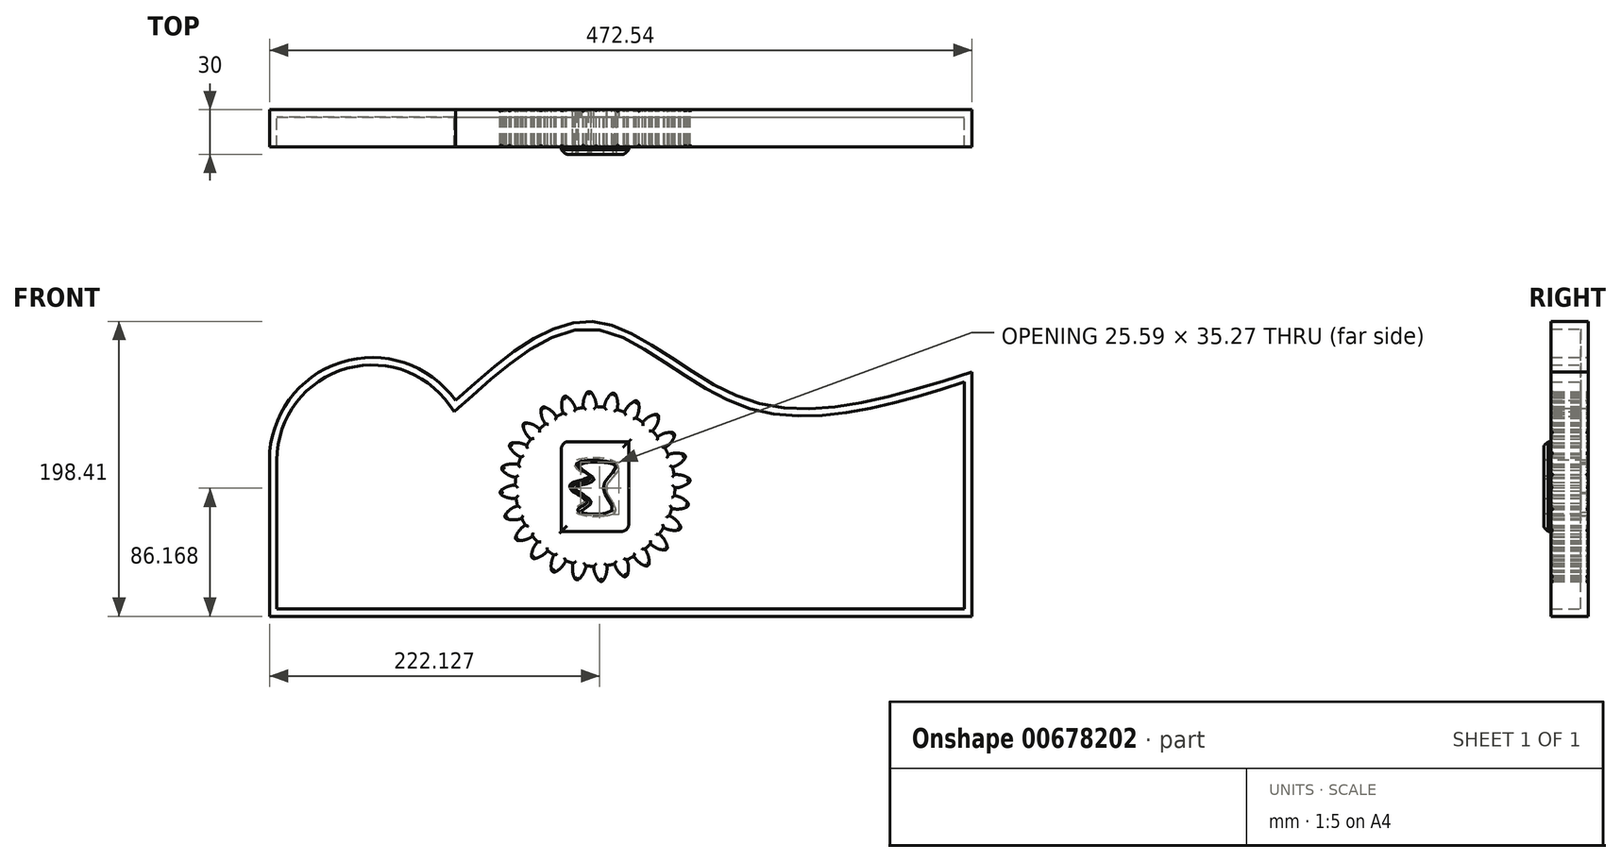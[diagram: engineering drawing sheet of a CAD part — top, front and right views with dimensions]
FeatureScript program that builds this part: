
annotation { "Feature Type Name" : "Feature", "Feature Type Description" : "" }
export const myFeature = defineFeature(function(context is Context, id is Id, definition is map)
    precondition{}
    {
        {
            var Q0;
            Q0=qCreatedBy(makeId("Front.planeOp"),FACE);
            var sketch = newSketch(context, id + "F0", { "sketchPlane" : qUnion([Q0])});
            skCircle(sketch, "E0", {"center": v(0, 0) * mm, "radius": 53.72 * mm});
            skCircle(sketch, "E1", {"center": v(0, 0) * mm, "radius": 58.67 * mm, "construction": true});
            skCircle(sketch, "E2", {"center": v(0, 0) * mm, "radius": 63.5 * mm, "construction": true});
            skLineSegment(sketch, "E3", {"start": v(0, 0) * mm, "end": v(0, 95.08) * mm, "construction": true});
            skLineSegment(sketch, "E4", {"start": v(0, 0) * mm, "end": v(-6.3, 96.03) * mm, "construction": true});
            skLineSegment(sketch, "E5", {"start": v(0, 63.95) * mm, "end": v(0, 63.5) * mm, "construction": true});
            skLineSegment(sketch, "E6", {"start": v(0, 58.67) * mm, "end": v(-63.97, 58.67) * mm, "construction": true});
            skLineSegment(sketch, "E7", {"start": v(0, 58.67) * mm, "end": v(-64.16, 35.32) * mm, "construction": true});
            skCircle(sketch, "E8", {"center": v(0, 0) * mm, "radius": 55.14 * mm, "construction": true});
            skCircle(sketch, "E9", {"center": v(0, 58.67) * mm, "radius": 14.6 * mm, "construction": true});
            skCircle(sketch, "E10", {"center": v(-13.72, 53.68) * mm, "radius": 14.6 * mm, "construction": true});
            skArc(sketch, "E11", {"start": v(0, 58.67) * mm, "mid": v(-1.2, 61.2) * mm, "end": v(-2.86, 63.44) * mm});
            skArc(sketch, "E12", {"start": v(0.88, 53.71) * mm, "mid": v(0.66, 56.23) * mm, "end": v(0, 58.67) * mm});
            skArc(sketch, "E13.MirrorCS", {"start": v(-7.66, 58.17) * mm, "mid": v(-6.8, 60.83) * mm, "end": v(-5.45, 63.27) * mm});
            skArc(sketch, "E14.MirrorCS", {"start": v(-7.88, 53.14) * mm, "mid": v(-7.99, 55.67) * mm, "end": v(-7.66, 58.17) * mm});
            skArc(sketch, "E15", {"start": v(-2.86, 63.44) * mm, "mid": v(-4.18, 63.85) * mm, "end": v(-5.45, 63.27) * mm});
            skLineSegment(sketch, "E16.bottom", {"start": v(22.6, 30.17) * mm, "end": v(-18.1, 30.17) * mm});
            skLineSegment(sketch, "E16.top", {"start": v(18.1, -30.17) * mm, "end": v(-22.6, -30.17) * mm});
            skLineSegment(sketch, "E16.left", {"start": v(22.6, 30.17) * mm, "end": v(22.6, -25.67) * mm});
            skLineSegment(sketch, "E16.right", {"start": v(-22.6, 25.67) * mm, "end": v(-22.6, -30.17) * mm});
            skFitSpline(sketch, "E17", {"points": [v(-11.69, -16.1) * mm, v(11.42, -16.15) * mm, v(5.58, 0) * mm, v(13.67, 14.65) * mm, v(-12.75, 15.4) * mm, v(-2.8, 5.83) * mm, v(-15.25, 0) * mm, v(-4.75, -9.12) * mm, v(-11.69, -16.1) * mm]});
            skPoint(sketch, "E18.visualSharp", {"position": v(-22.6, 30.17) * mm});
            skArc(sketch, "E18.filletArc", {"start": v(-18.1, 30.17) * mm, "mid": v(-21.28, 28.85) * mm, "end": v(-22.6, 25.67) * mm});
            skPoint(sketch, "E19.visualSharp", {"position": v(22.6, -30.17) * mm});
            skArc(sketch, "E19.filletArc", {"start": v(18.1, -30.17) * mm, "mid": v(21.28, -28.85) * mm, "end": v(22.6, -25.67) * mm});
            skSolve(sketch);
        }
        {
            var Q0;
            {var subQ0=sQuery(id+"F0.wireOp",EDGE,"E0");var subQ1=makeQuery(id+"F0.imprint","INTERSECT",VERTEX,{"derivedFrom":[subQ0,sQuery(id+"F0.wireOp",EDGE,"E12")]});Q0=makeQuery(id+"F0.imprint","IMPRINT",FACE,{"disambiguationData":[TD([[makeQuery(id+"F0.imprint","IMPRINT",EDGE,{"disambiguationData":[TD([[subQ1,-1.0]])],"derivedFrom":subQ0}),1.0]])]});}
            var Q1;
            Q1=makeQuery(id+"F0.imprint","IMPRINT",FACE,{"disambiguationData":[TD([[makeQuery(id+"F0.imprint","IMPRINT",EDGE,{"derivedFrom":sQuery(id+"F0.wireOp",EDGE,"E11")}),1.0]])]});
            extrude(context, id + "F1", {"entities" : qUnion([Q0, Q1]), "depth" : 25 * mm, "offsetDistance" : 25 * mm});
        }
        {
            var Q0;
            Q0=makeQuery(id+"F1.opExtrude","SWEPT_BODY",BODY,{"disambiguationData":[OSD([sQuery(id+"F0.wireOp",EDGE,"E0"),sQuery(id+"F0.wireOp",EDGE,"E11"),sQuery(id+"F0.wireOp",EDGE,"E12"),sQuery(id+"F0.wireOp",EDGE,"E13.MirrorCS"),sQuery(id+"F0.wireOp",EDGE,"E14.MirrorCS"),sQuery(id+"F0.wireOp",EDGE,"E15")])]});
            var Q1;
            Q1=makeQuery(id+"F1.opExtrude","SWEPT_FACE",FACE,{"disambiguationData":[OSD([sQuery(id+"F0.wireOp",EDGE,"E0")])]});
            circularPattern(context, id + "F2", {"entities" : qUnion([Q0]), "axis" : qUnion([Q1]), "angle" : 360 * degree, "instanceCount" : 24, "equalSpace" : true});
        }
        {
            var Q0;
            Q0=makeQuery(id+"F0.imprint","IMPRINT",FACE,{"disambiguationData":[TD([[makeQuery(id+"F0.imprint","IMPRINT",EDGE,{"derivedFrom":sQuery(id+"F0.wireOp",EDGE,"E16.bottom")}),1.0]])]});
            extrude(context, id + "F3", {"entities" : qUnion([Q0]), "operationType" : NewBodyOperationType.ADD, "depth" : 30 * mm, "offsetDistance" : 25 * mm});
        }
        {
            var Q0;
            Q0=makeQuery(id+"F3.opExtrude","CAP_EDGE",EDGE,{"disambiguationData":[OSD([sQuery(id+"F0.wireOp",EDGE,"E16.bottom")])],"isStart":false});
            var Q1;
            Q1=makeQuery(id+"F3.opExtrude","CAP_EDGE",EDGE,{"disambiguationData":[OSD([sQuery(id+"F0.wireOp",EDGE,"E16.right")])],"isStart":false});
            var Q2;
            Q2=makeQuery(id+"F3.opExtrude","CAP_EDGE",EDGE,{"disambiguationData":[OSD([sQuery(id+"F0.wireOp",EDGE,"E16.left")])],"isStart":false});
            var Q3;
            Q3=makeQuery(id+"F3.opExtrude","CAP_EDGE",EDGE,{"disambiguationData":[OSD([sQuery(id+"F0.wireOp",EDGE,"E16.top")])],"isStart":false});
            var Q4;
            Q4=makeQuery(id+"F3.opExtrude","CAP_EDGE",EDGE,{"disambiguationData":[OSD([sQuery(id+"F0.wireOp",EDGE,"E16.bottom")])],"isStart":true});
            var Q5;
            Q5=makeQuery(id+"F3.opExtrude","CAP_EDGE",EDGE,{"disambiguationData":[OSD([sQuery(id+"F0.wireOp",EDGE,"E16.top")])],"isStart":true});
            chamfer(context, id + "F4", {"entities" : qUnion([Q0, Q1, Q2, Q3, Q4, Q5]), "width" : 3 * mm, "tangentPropagation" : true});
        }
        {
            var Q0;
            {var subQ0=sQuery(id+"F0.wireOp",EDGE,"E19.filletArc");var subQ1=sQuery(id+"F0.wireOp",EDGE,"E18.filletArc");var subQ2=sQuery(id+"F0.wireOp",EDGE,"E16.right");var subQ3=sQuery(id+"F0.wireOp",EDGE,"E16.left");var subQ4=sQuery(id+"F0.wireOp",EDGE,"E16.top");var subQ5=sQuery(id+"F0.wireOp",EDGE,"E16.bottom");var subQ6=makeQuery(id+"F1.opExtrude","CAP_FACE",FACE,{"disambiguationData":[OSD([sQuery(id+"F0.wireOp",EDGE,"E0"),sQuery(id+"F0.wireOp",EDGE,"E11"),sQuery(id+"F0.wireOp",EDGE,"E12"),sQuery(id+"F0.wireOp",EDGE,"E13.MirrorCS"),sQuery(id+"F0.wireOp",EDGE,"E14.MirrorCS"),sQuery(id+"F0.wireOp",EDGE,"E15"),subQ5,subQ4,subQ3,subQ2,subQ1,subQ0])],"isStart":true});Q0=makeQuery(id+"F3.boolean.opBoolean","MERGE",FACE,{"derivedFrom":[subQ6,makeQuery(id+"F2.opPattern","COPY",FACE,{"derivedFrom":subQ6,"instanceName":"1"}),makeQuery(id+"F2.opPattern","COPY",FACE,{"derivedFrom":subQ6,"instanceName":"2"}),makeQuery(id+"F2.opPattern","COPY",FACE,{"derivedFrom":subQ6,"instanceName":"3"}),makeQuery(id+"F2.opPattern","COPY",FACE,{"derivedFrom":subQ6,"instanceName":"4"}),makeQuery(id+"F2.opPattern","COPY",FACE,{"derivedFrom":subQ6,"instanceName":"5"}),makeQuery(id+"F2.opPattern","COPY",FACE,{"derivedFrom":subQ6,"instanceName":"6"}),makeQuery(id+"F2.opPattern","COPY",FACE,{"derivedFrom":subQ6,"instanceName":"7"}),makeQuery(id+"F2.opPattern","COPY",FACE,{"derivedFrom":subQ6,"instanceName":"8"}),makeQuery(id+"F2.opPattern","COPY",FACE,{"derivedFrom":subQ6,"instanceName":"9"}),makeQuery(id+"F2.opPattern","COPY",FACE,{"derivedFrom":subQ6,"instanceName":"10"}),makeQuery(id+"F2.opPattern","COPY",FACE,{"derivedFrom":subQ6,"instanceName":"11"}),makeQuery(id+"F2.opPattern","COPY",FACE,{"derivedFrom":subQ6,"instanceName":"12"}),makeQuery(id+"F2.opPattern","COPY",FACE,{"derivedFrom":subQ6,"instanceName":"13"}),makeQuery(id+"F2.opPattern","COPY",FACE,{"derivedFrom":subQ6,"instanceName":"14"}),makeQuery(id+"F2.opPattern","COPY",FACE,{"derivedFrom":subQ6,"instanceName":"15"}),makeQuery(id+"F2.opPattern","COPY",FACE,{"derivedFrom":subQ6,"instanceName":"16"}),makeQuery(id+"F2.opPattern","COPY",FACE,{"derivedFrom":subQ6,"instanceName":"17"}),makeQuery(id+"F2.opPattern","COPY",FACE,{"derivedFrom":subQ6,"instanceName":"18"}),makeQuery(id+"F2.opPattern","COPY",FACE,{"derivedFrom":subQ6,"instanceName":"19"}),makeQuery(id+"F2.opPattern","COPY",FACE,{"derivedFrom":subQ6,"instanceName":"20"}),makeQuery(id+"F2.opPattern","COPY",FACE,{"derivedFrom":subQ6,"instanceName":"21"}),makeQuery(id+"F2.opPattern","COPY",FACE,{"derivedFrom":subQ6,"instanceName":"22"}),makeQuery(id+"F2.opPattern","COPY",FACE,{"derivedFrom":subQ6,"instanceName":"23"}),makeQuery(id+"F3.opExtrude","CAP_FACE",FACE,{"disambiguationData":[OSD([subQ5,subQ4,subQ3,subQ2,sQuery(id+"F0.wireOp",EDGE,"E17"),subQ1,subQ0])],"isStart":true})]});}
            var Q1;
            {var subQ0=makeQuery(id+"F1.opExtrude","CAP_FACE",FACE,{"disambiguationData":[OSD([sQuery(id+"F0.wireOp",EDGE,"E0"),sQuery(id+"F0.wireOp",EDGE,"E11"),sQuery(id+"F0.wireOp",EDGE,"E12"),sQuery(id+"F0.wireOp",EDGE,"E13.MirrorCS"),sQuery(id+"F0.wireOp",EDGE,"E14.MirrorCS"),sQuery(id+"F0.wireOp",EDGE,"E15"),sQuery(id+"F0.wireOp",EDGE,"E16.bottom"),sQuery(id+"F0.wireOp",EDGE,"E16.top"),sQuery(id+"F0.wireOp",EDGE,"E16.left"),sQuery(id+"F0.wireOp",EDGE,"E16.right"),sQuery(id+"F0.wireOp",EDGE,"E18.filletArc"),sQuery(id+"F0.wireOp",EDGE,"E19.filletArc")])],"isStart":false});Q1=makeQuery(id+"F3.boolean.opBoolean","MERGE",FACE,{"derivedFrom":[subQ0,makeQuery(id+"F2.opPattern","COPY",FACE,{"derivedFrom":subQ0,"instanceName":"1"}),makeQuery(id+"F2.opPattern","COPY",FACE,{"derivedFrom":subQ0,"instanceName":"2"}),makeQuery(id+"F2.opPattern","COPY",FACE,{"derivedFrom":subQ0,"instanceName":"3"}),makeQuery(id+"F2.opPattern","COPY",FACE,{"derivedFrom":subQ0,"instanceName":"4"}),makeQuery(id+"F2.opPattern","COPY",FACE,{"derivedFrom":subQ0,"instanceName":"5"}),makeQuery(id+"F2.opPattern","COPY",FACE,{"derivedFrom":subQ0,"instanceName":"6"}),makeQuery(id+"F2.opPattern","COPY",FACE,{"derivedFrom":subQ0,"instanceName":"7"}),makeQuery(id+"F2.opPattern","COPY",FACE,{"derivedFrom":subQ0,"instanceName":"8"}),makeQuery(id+"F2.opPattern","COPY",FACE,{"derivedFrom":subQ0,"instanceName":"9"}),makeQuery(id+"F2.opPattern","COPY",FACE,{"derivedFrom":subQ0,"instanceName":"10"}),makeQuery(id+"F2.opPattern","COPY",FACE,{"derivedFrom":subQ0,"instanceName":"11"}),makeQuery(id+"F2.opPattern","COPY",FACE,{"derivedFrom":subQ0,"instanceName":"12"}),makeQuery(id+"F2.opPattern","COPY",FACE,{"derivedFrom":subQ0,"instanceName":"13"}),makeQuery(id+"F2.opPattern","COPY",FACE,{"derivedFrom":subQ0,"instanceName":"14"}),makeQuery(id+"F2.opPattern","COPY",FACE,{"derivedFrom":subQ0,"instanceName":"15"}),makeQuery(id+"F2.opPattern","COPY",FACE,{"derivedFrom":subQ0,"instanceName":"16"}),makeQuery(id+"F2.opPattern","COPY",FACE,{"derivedFrom":subQ0,"instanceName":"17"}),makeQuery(id+"F2.opPattern","COPY",FACE,{"derivedFrom":subQ0,"instanceName":"18"}),makeQuery(id+"F2.opPattern","COPY",FACE,{"derivedFrom":subQ0,"instanceName":"19"}),makeQuery(id+"F2.opPattern","COPY",FACE,{"derivedFrom":subQ0,"instanceName":"20"}),makeQuery(id+"F2.opPattern","COPY",FACE,{"derivedFrom":subQ0,"instanceName":"21"}),makeQuery(id+"F2.opPattern","COPY",FACE,{"derivedFrom":subQ0,"instanceName":"22"}),makeQuery(id+"F2.opPattern","COPY",FACE,{"derivedFrom":subQ0,"instanceName":"23"})]});}
            fillet(context, id + "F5", {"entities" : qUnion([Q0, Q1]), "radius" : 1.5 * mm, "tangentPropagation" : true, "allowEdgeOverflow" : false});
        }
        {
            var Q0;
            Q0=makeQuery(id+"F3.opExtrude","SWEPT_FACE",FACE,{"disambiguationData":[OSD([sQuery(id+"F0.wireOp",EDGE,"E17")])]});
            var Q1;
            {var subQ0=sQuery(id+"F0.wireOp",EDGE,"E16.bottom");Q1=makeQuery(id+"F4.opChamfer","BLEND_EDGE",EDGE,{"blendedFrom":[makeQuery(id+"F3.opExtrude","CAP_EDGE",EDGE,{"disambiguationData":[OSD([subQ0])],"isStart":false}),makeQuery(id+"F3.opExtrude","CAP_FACE",FACE,{"disambiguationData":[OSD([subQ0,sQuery(id+"F0.wireOp",EDGE,"E16.top"),sQuery(id+"F0.wireOp",EDGE,"E16.left"),sQuery(id+"F0.wireOp",EDGE,"E16.right"),sQuery(id+"F0.wireOp",EDGE,"E17"),sQuery(id+"F0.wireOp",EDGE,"E18.filletArc"),sQuery(id+"F0.wireOp",EDGE,"E19.filletArc")])],"isStart":false})],"blendedInto":[makeQuery(id+"F3.opExtrude","CAP_FACE",FACE,{"disambiguationData":[OSD([subQ0,sQuery(id+"F0.wireOp",EDGE,"E16.top"),sQuery(id+"F0.wireOp",EDGE,"E16.left"),sQuery(id+"F0.wireOp",EDGE,"E16.right"),sQuery(id+"F0.wireOp",EDGE,"E17"),sQuery(id+"F0.wireOp",EDGE,"E18.filletArc"),sQuery(id+"F0.wireOp",EDGE,"E19.filletArc")])],"isStart":false})]});}
            var Q2;
            {var subQ0=sQuery(id+"F0.wireOp",EDGE,"E16.left");Q2=makeQuery(id+"F4.opChamfer","BLEND_EDGE",EDGE,{"blendedFrom":[makeQuery(id+"F3.opExtrude","CAP_EDGE",EDGE,{"disambiguationData":[OSD([subQ0])],"isStart":false}),makeQuery(id+"F3.opExtrude","CAP_FACE",FACE,{"disambiguationData":[OSD([sQuery(id+"F0.wireOp",EDGE,"E16.bottom"),sQuery(id+"F0.wireOp",EDGE,"E16.top"),subQ0,sQuery(id+"F0.wireOp",EDGE,"E16.right"),sQuery(id+"F0.wireOp",EDGE,"E17"),sQuery(id+"F0.wireOp",EDGE,"E18.filletArc"),sQuery(id+"F0.wireOp",EDGE,"E19.filletArc")])],"isStart":false})],"blendedInto":[makeQuery(id+"F3.opExtrude","CAP_FACE",FACE,{"disambiguationData":[OSD([sQuery(id+"F0.wireOp",EDGE,"E16.bottom"),sQuery(id+"F0.wireOp",EDGE,"E16.top"),subQ0,sQuery(id+"F0.wireOp",EDGE,"E16.right"),sQuery(id+"F0.wireOp",EDGE,"E17"),sQuery(id+"F0.wireOp",EDGE,"E18.filletArc"),sQuery(id+"F0.wireOp",EDGE,"E19.filletArc")])],"isStart":false})]});}
            var Q3;
            {var subQ0=sQuery(id+"F0.wireOp",EDGE,"E16.top");Q3=makeQuery(id+"F4.opChamfer","BLEND_EDGE",EDGE,{"blendedFrom":[makeQuery(id+"F3.opExtrude","CAP_EDGE",EDGE,{"disambiguationData":[OSD([subQ0])],"isStart":false}),makeQuery(id+"F3.opExtrude","CAP_FACE",FACE,{"disambiguationData":[OSD([sQuery(id+"F0.wireOp",EDGE,"E16.bottom"),subQ0,sQuery(id+"F0.wireOp",EDGE,"E16.left"),sQuery(id+"F0.wireOp",EDGE,"E16.right"),sQuery(id+"F0.wireOp",EDGE,"E17"),sQuery(id+"F0.wireOp",EDGE,"E18.filletArc"),sQuery(id+"F0.wireOp",EDGE,"E19.filletArc")])],"isStart":false})],"blendedInto":[makeQuery(id+"F3.opExtrude","CAP_FACE",FACE,{"disambiguationData":[OSD([sQuery(id+"F0.wireOp",EDGE,"E16.bottom"),subQ0,sQuery(id+"F0.wireOp",EDGE,"E16.left"),sQuery(id+"F0.wireOp",EDGE,"E16.right"),sQuery(id+"F0.wireOp",EDGE,"E17"),sQuery(id+"F0.wireOp",EDGE,"E18.filletArc"),sQuery(id+"F0.wireOp",EDGE,"E19.filletArc")])],"isStart":false})]});}
            var Q4;
            {var subQ0=sQuery(id+"F0.wireOp",EDGE,"E16.right");Q4=makeQuery(id+"F4.opChamfer","BLEND_EDGE",EDGE,{"blendedFrom":[makeQuery(id+"F3.opExtrude","CAP_EDGE",EDGE,{"disambiguationData":[OSD([subQ0])],"isStart":false}),makeQuery(id+"F3.opExtrude","CAP_FACE",FACE,{"disambiguationData":[OSD([sQuery(id+"F0.wireOp",EDGE,"E16.bottom"),sQuery(id+"F0.wireOp",EDGE,"E16.top"),sQuery(id+"F0.wireOp",EDGE,"E16.left"),subQ0,sQuery(id+"F0.wireOp",EDGE,"E17"),sQuery(id+"F0.wireOp",EDGE,"E18.filletArc"),sQuery(id+"F0.wireOp",EDGE,"E19.filletArc")])],"isStart":false})],"blendedInto":[makeQuery(id+"F3.opExtrude","CAP_FACE",FACE,{"disambiguationData":[OSD([sQuery(id+"F0.wireOp",EDGE,"E16.bottom"),sQuery(id+"F0.wireOp",EDGE,"E16.top"),sQuery(id+"F0.wireOp",EDGE,"E16.left"),subQ0,sQuery(id+"F0.wireOp",EDGE,"E17"),sQuery(id+"F0.wireOp",EDGE,"E18.filletArc"),sQuery(id+"F0.wireOp",EDGE,"E19.filletArc")])],"isStart":false})]});}
            fillet(context, id + "F6", {"entities" : qUnion([Q0, Q1, Q2, Q3, Q4]), "radius" : 1.75 * mm, "tangentPropagation" : true, "allowEdgeOverflow" : false});
        }
        {
            var Q0;
            Q0=qCreatedBy(makeId("Front.planeOp"),FACE);
            var sketch = newSketch(context, id + "F7", { "sketchPlane" : qUnion([Q0])});
            skLineSegment(sketch, "E20", {"start": v(-219.06, -87.36) * mm, "end": v(253.48, -87.36) * mm});
            skLineSegment(sketch, "E21", {"start": v(253.48, -87.36) * mm, "end": v(253.48, 77.1) * mm});
            skLineSegment(sketch, "E22", {"start": v(-219.06, -87.36) * mm, "end": v(-219.06, 17.74) * mm});
            skArc(sketch, "E23", {"start": v(-219.06, 17.74) * mm, "mid": v(-171.12, 83.45) * mm, "end": v(-93.9, 57.85) * mm});
            skFitSpline(sketch, "E24", {"points": [v(-93.9, 57.85) * mm, v(0, 110.8) * mm, v(103.45, 57.85) * mm, v(253.48, 77.1) * mm], "startDerivative": vector(303.13, 271.22) * mm, "endDerivative": vector(431.52, 137.96) * mm});
            skSolve(sketch);
        }
        {
            var Q0;
            Q0=makeQuery(id+"F7.imprint","IMPRINT",FACE,{"disambiguationData":[TD([[makeQuery(id+"F7.imprint","IMPRINT",EDGE,{"derivedFrom":sQuery(id+"F7.wireOp",EDGE,"E20")}),1.0]])]});
            extrude(context, id + "F8", {"entities" : qUnion([Q0]), "depth" : 25 * mm, "offsetDistance" : 25 * mm});
        }
        {
            var Q0;
            Q0=makeQuery(id+"F8.opExtrude","CAP_FACE",FACE,{"disambiguationData":[OSD([sQuery(id+"F7.wireOp",EDGE,"E20"),sQuery(id+"F7.wireOp",EDGE,"E21"),sQuery(id+"F7.wireOp",EDGE,"E22"),sQuery(id+"F7.wireOp",EDGE,"E23"),sQuery(id+"F7.wireOp",EDGE,"E24")])],"isStart":false});
            shell(context, id + "F9", {"entities" : qUnion([Q0]), "thickness" : 5 * mm});
        }
        {
            var Q0;
            Q0=makeQuery(id+"F9.opShell","OFFSET_FACE",FACE,{"disambiguationData":[OSD([sQuery(id+"F7.wireOp",EDGE,"E20"),sQuery(id+"F7.wireOp",EDGE,"E21"),sQuery(id+"F7.wireOp",EDGE,"E22"),sQuery(id+"F7.wireOp",EDGE,"E23"),sQuery(id+"F7.wireOp",EDGE,"E24")])]});
            var sketch = newSketch(context, id + "F10", { "sketchPlane" : qUnion([Q0])});
            skFitSpline(sketch, "E25", {"points": [v(-9.58, -17.36) * mm, v(13.53, -17.42) * mm, v(7.7, -1.27) * mm, v(15.78, 13.38) * mm, v(-10.64, 14.12) * mm, v(-0.7, 4.55) * mm, v(-13.14, -1.27) * mm, v(-2.64, -10.4) * mm, v(-9.58, -17.36) * mm]});
            skSolve(sketch);
        }
        {
            var Q0;
            Q0=makeQuery(id+"F10.imprint","IMPRINT",FACE,{"disambiguationData":[TD([[makeQuery(id+"F10.imprint","IMPRINT",EDGE,{"derivedFrom":sQuery(id+"F10.wireOp",EDGE,"E25")}),1.0]])]});
            extrude(context, id + "F11", {"entities" : qUnion([Q0]), "operationType" : NewBodyOperationType.REMOVE, "oppositeDirection" : true, "depth" : 5.1 * mm, "offsetDistance" : 25 * mm});
        }
    });
